# Revit family: Paper_Holder-Grohe-StarLight-41067_Series
name_source: partatom
category: Plumbing Fixtures
revit_build: Autodesk Revit 2016 (Build: 20150714_1515(x64)
units: mm (PartAtom-declared; Revit-internal decimal feet)

## family parameters
Cut with Voids When Loaded = No
Host = Face
Part Type = Normal
Room Calculation Point = No
Round Connector Dimension = Use Diameter
Shared = Yes

## types (5) — shared parameters
CW Connection = No
Default Elevation = 0"
Description = Paper Holder
HW Connection = No
Height = 9 7/16"
Installation Type = Wall
Length = 2 7/16"
Manufacturer = Grohe
Price = Prices may vary. Please consult Manufacturer Representative for most up-to-date price list.
URL = https://www.grohe.us
Vent Connection = No
Waste Connection = No
Width = 9/16"
zero-valued in all types: CWFU, HWFU, WFU

## per-type parameters (varying)
| type | Finish |
| 41067000 | Metal-Grohe-000-StarLight Chrome |
| 41067A00 | Metal-Grohe-A00-Hard Graphite |
| 41067BE0 | Metal-Grohe-BE0-Polished Nickel InfinityFinish |
| 41067EN0 | Metal-Grohe-EN0-Brushed Nickel InfinityFinish |
| 41067GN0 | Metal-Grohe-GN0-Brushed Cool Sunrise |

note: column(s) folded — value = type name in every type: Model

## geometry (parser evidence)
native form markers: Sweep x3
no freeform markers — native parametric forms only
